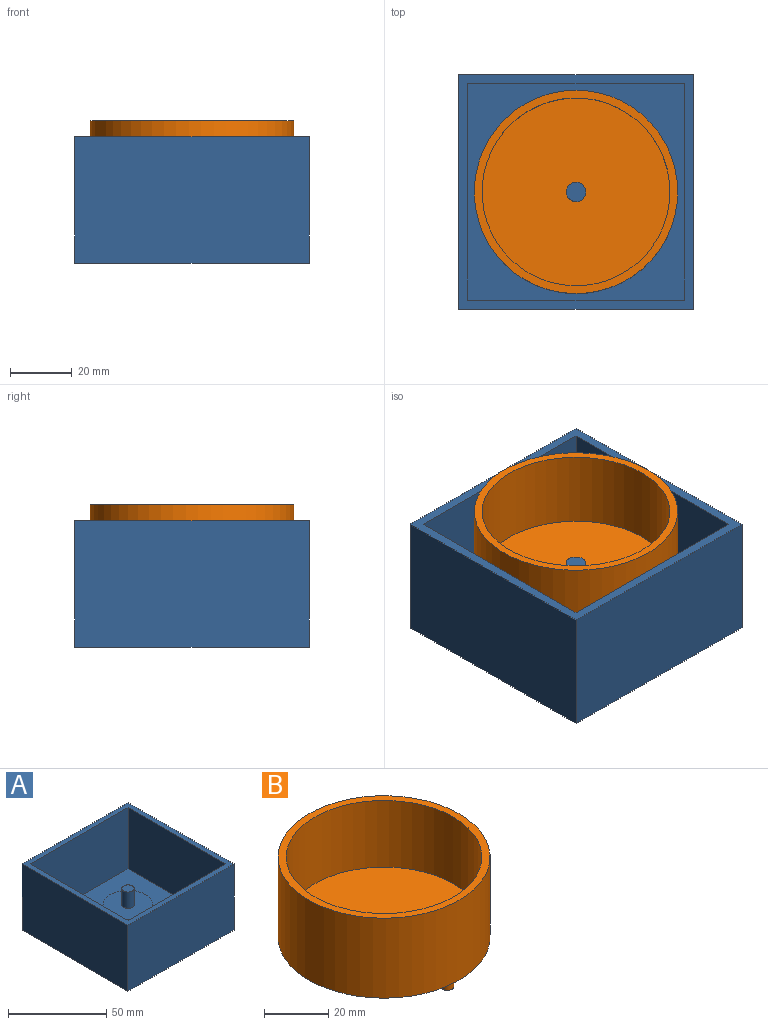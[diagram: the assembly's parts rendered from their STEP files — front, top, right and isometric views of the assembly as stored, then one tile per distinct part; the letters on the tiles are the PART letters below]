
ASSEMBLY  parts=2 mates=1
PART A: 15 faces, bbox 76.2x76.2x41.1 mm
  f0: plane 76.2x41.1mm, normal (1,0,0), area 3131.8mm2, adj f1,f3,f4,f9
  f1: plane 76.2x41.1mm, normal (0,1,0), area 3131.8mm2, adj f0,f2,f4,f9
  f2: plane 76.2x41.1mm, normal (-1,0,0), area 3131.8mm2, adj f1,f3,f4,f9
  f3: plane 76.2x41.1mm, normal (0,-1,0), area 3131.8mm2, adj f0,f2,f4,f9
  f4: plane 76.2x76.2mm, normal (0,0,-1), area 5806.4mm2, adj f0,f1,f2,f3
  f5: plane 70.2x38.1mm, normal (1,0,0), area 2674.6mm2, adj f6,f8,f9,f10
  f6: plane 70.2x38.1mm, normal (0,-1,0), area 2674.6mm2, adj f5,f7,f9,f10
  f7: plane 70.2x38.1mm, normal (-1,0,0), area 2674.6mm2, adj f6,f8,f9,f10
  f8: plane 70.2x38.1mm, normal (0,1,0), area 2674.6mm2, adj f5,f7,f9,f10
  f9: plane 76.2x76.2mm, normal (0,0,1), area 878.4mm2, adj f0,f1,f2,f3,f5,f6,f7,f8
  f10: plane 70.2x70.2mm, normal (0,0,1), area 4421.3mm2, adj f5,f6,f7,f8,f11
  f11: cylinder r=12.7mm len=25.4mm, axis (0,0,-1), area 1013.4mm2, adj f10,f12
  f12: plane 25.4x25.4mm, normal (0,0,1), area 475mm2, adj f11,f13
  f13: cylinder r=3.17mm len=10.16mm, axis (0,0,-1), area 202.7mm2, adj f12,f14
  f14: plane 6.35x6.35mm, normal (0,0,1), area 31.7mm2, adj f13
PART B: 8 faces, bbox 66x66x35.6 mm
  f0: plane 60.96x60.96mm, normal (0,0,1), area 2887mm2, adj f1,f4
  f1: cylinder r=3.17mm len=6.35mm, axis (0,0,-1), area 101.3mm2, adj f0,f3
  f2: cylinder r=33.02mm len=66.04mm, axis (0,0,-1), area 6323.7mm2, adj f3,f5
  f3: plane 66.04x66.04mm, normal (0,0,-1), area 3382.3mm2, adj f1,f2,f6
  f4: cylinder r=30.48mm len=60.96mm, axis (0,0,-1), area 4864.4mm2, adj f0,f5
  f5: plane 66.04x66.04mm, normal (0,0,1), area 506.7mm2, adj f2,f4
  f6: cylinder r=1.91mm len=5.08mm, axis (0,0,1), area 60.8mm2, adj f3,f7
  f7: plane 3.81x3.81mm, normal (0,0,-1), area 11.4mm2, adj f6
PLACE A t=(-0.63,0,0)mm
PLACE B t=(-38.74,38.1,15.7)mm
MATE revolute B.f1 <-> A.f11  axis (0,0,-1) through (-38.74,38.1,15.7)mm
